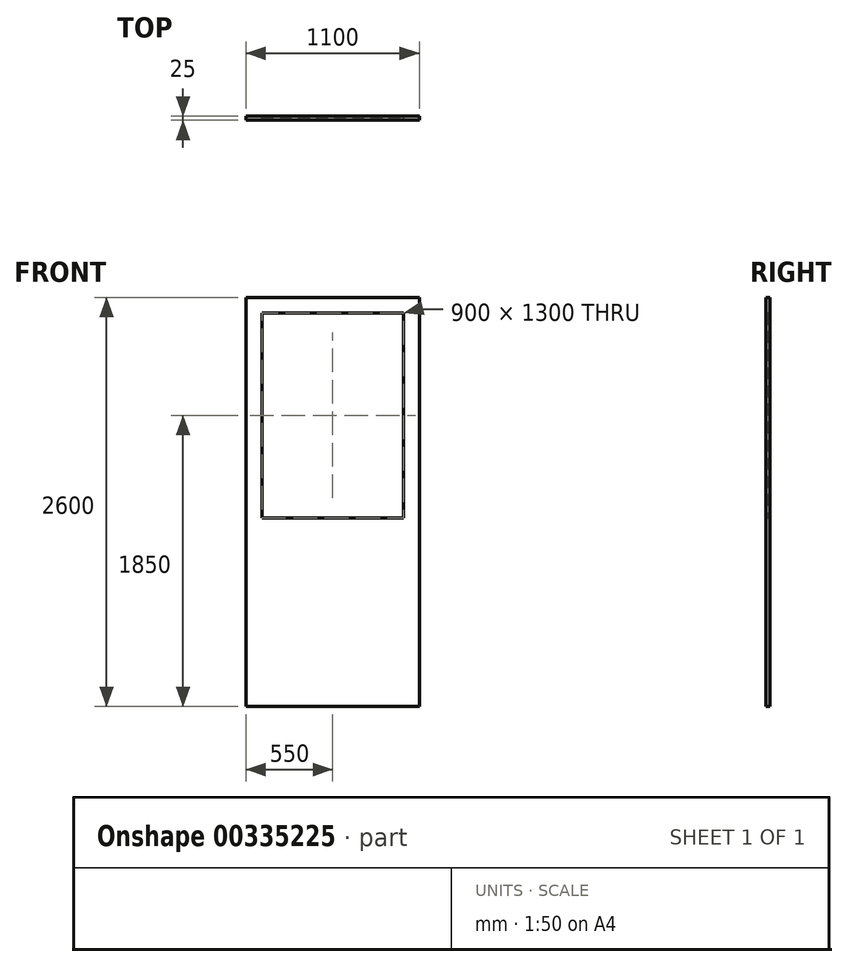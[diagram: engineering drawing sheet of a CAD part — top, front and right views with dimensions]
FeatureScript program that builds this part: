
annotation { "Feature Type Name" : "Feature", "Feature Type Description" : "" }
export const myFeature = defineFeature(function(context is Context, id is Id, definition is map)
    precondition{}
    {
        {
            var Q0;
            Q0=qCreatedBy(makeId("Front.planeOp"),FACE);
            var sketch = newSketch(context, id + "F0", { "sketchPlane" : qUnion([Q0])});
            skLineSegment(sketch, "E0.bottom", {"start": v(550, 0) * mm, "end": v(-550, 0) * mm});
            skLineSegment(sketch, "E0.top", {"start": v(550, 2600) * mm, "end": v(-550, 2600) * mm});
            skLineSegment(sketch, "E0.left", {"start": v(550, 0) * mm, "end": v(550, 2600) * mm});
            skLineSegment(sketch, "E0.right", {"start": v(-550, 0) * mm, "end": v(-550, 2600) * mm});
            skPoint(sketch, "E0.middle", {"position": v(0, 1300) * mm});
            skSolve(sketch);
        }
        {
            var Q0;
            Q0 = qSketchRegion(id + "F0", true);
            extrude(context, id + "F1", {"entities" : qUnion([Q0]), "endBound" : BoundingType.SYMMETRIC, "depth" : 25 * mm});
        }
        {
            var Q0;
            Q0=qCreatedBy(makeId("Front.planeOp"),FACE);
            var sketch = newSketch(context, id + "F2", { "sketchPlane" : qUnion([Q0])});
            skLineSegment(sketch, "E1.bottom", {"start": v(450, 2500) * mm, "end": v(-450, 2500) * mm});
            skLineSegment(sketch, "E1.top", {"start": v(450, 1200) * mm, "end": v(-450, 1200) * mm});
            skLineSegment(sketch, "E1.left", {"start": v(450, 2500) * mm, "end": v(450, 1200) * mm});
            skLineSegment(sketch, "E1.right", {"start": v(-450, 2500) * mm, "end": v(-450, 1200) * mm});
            skPoint(sketch, "E1.middle", {"position": v(0, 1850) * mm});
            skSolve(sketch);
        }
        {
            var Q0;
            Q0 = qSketchRegion(id + "F2", true);
            extrude(context, id + "F3", {"entities" : qUnion([Q0]), "operationType" : NewBodyOperationType.REMOVE, "endBound" : BoundingType.THROUGH_ALL, "oppositeDirection" : true, "depth" : 25 * mm, "hasSecondDirection" : true, "secondDirectionBound" : SecondDirectionBoundingType.THROUGH_ALL, "secondDirectionOppositeDirection" : false, "secondDirectionDepth" : 25 * mm});
        }
        {
            var Q0;
            Q0=qCreatedBy(makeId("Front.planeOp"),FACE);
            var sketch = newSketch(context, id + "F4", { "sketchPlane" : qUnion([Q0])});
            skLineSegment(sketch, "E2.bottom", {"start": v(-450, 2500) * mm, "end": v(450, 2500) * mm});
            skLineSegment(sketch, "E2.top", {"start": v(-450, 1200) * mm, "end": v(450, 1200) * mm});
            skLineSegment(sketch, "E2.left", {"start": v(-450, 2500) * mm, "end": v(-450, 1200) * mm});
            skLineSegment(sketch, "E2.right", {"start": v(450, 2500) * mm, "end": v(450, 1200) * mm});
            skSolve(sketch);
        }
        {
            var Q0;
            Q0 = qSketchRegion(id + "F4", true);
            extrude(context, id + "F5", {"entities" : qUnion([Q0]), "endBound" : BoundingType.SYMMETRIC, "depth" : 5 * mm});
        }
    });
